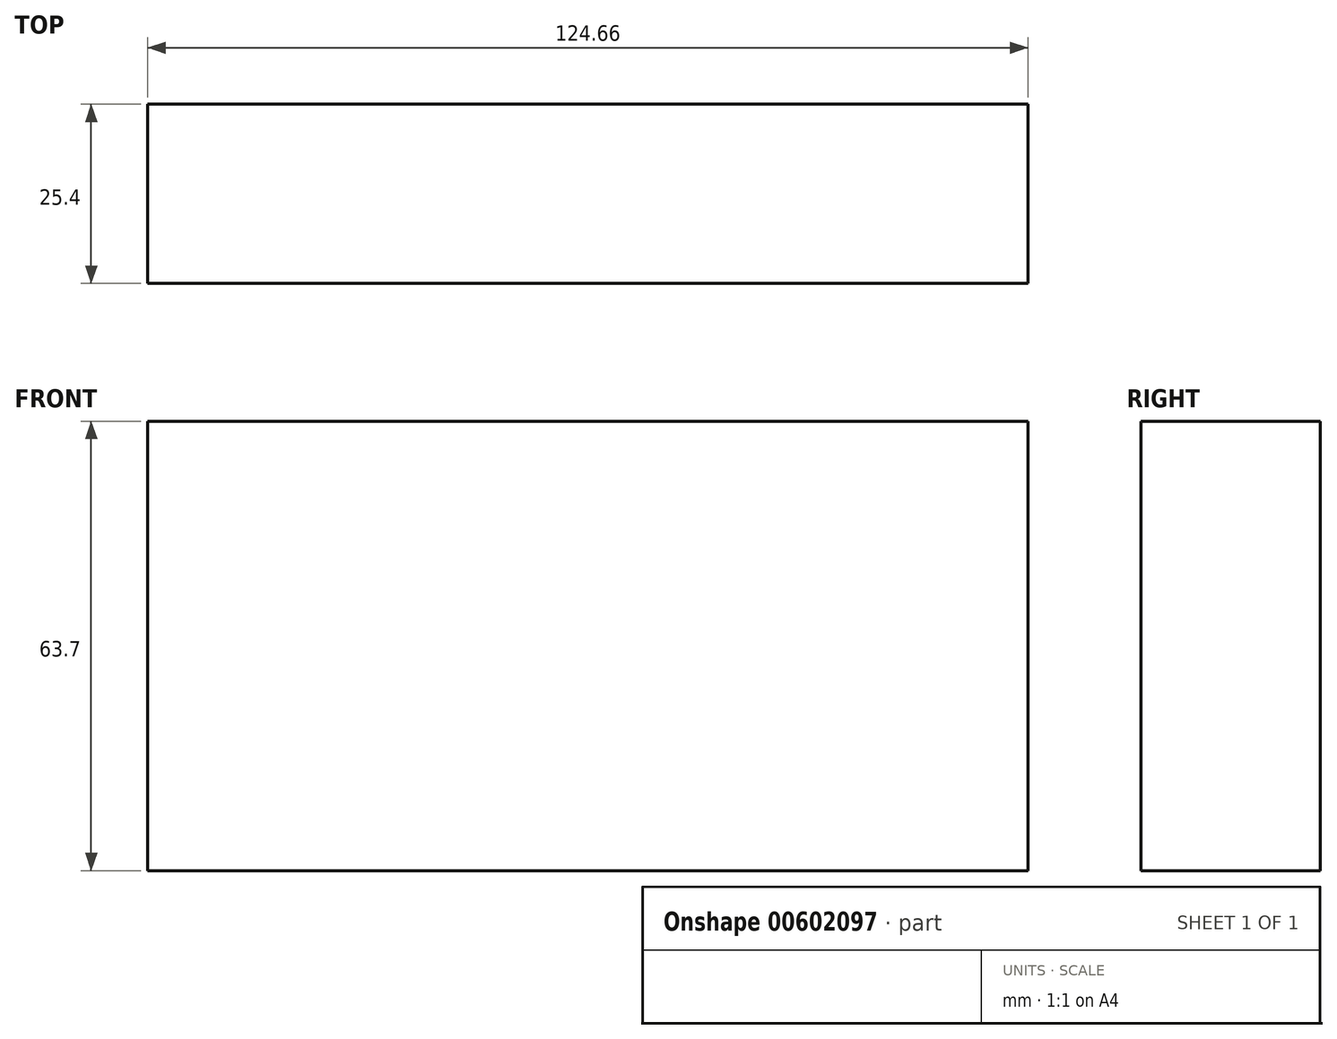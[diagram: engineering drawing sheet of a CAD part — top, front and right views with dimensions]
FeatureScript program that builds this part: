
annotation { "Feature Type Name" : "Feature", "Feature Type Description" : "" }
export const myFeature = defineFeature(function(context is Context, id is Id, definition is map)
    precondition{}
    {
        {
            var Q0;
            Q0=qCreatedBy(makeId("Front.planeOp"),FACE);
            var sketch = newSketch(context, id + "F0", { "sketchPlane" : qUnion([Q0])});
            skLineSegment(sketch, "E0.bottom", {"start": v(-55.32, 32.92) * mm, "end": v(69.34, 32.92) * mm});
            skLineSegment(sketch, "E0.top", {"start": v(-55.32, -30.78) * mm, "end": v(69.34, -30.78) * mm});
            skLineSegment(sketch, "E0.left", {"start": v(-55.32, 32.92) * mm, "end": v(-55.32, -30.78) * mm});
            skLineSegment(sketch, "E0.right", {"start": v(69.34, 32.92) * mm, "end": v(69.34, -30.78) * mm});
            skSolve(sketch);
        }
        {
            var Q0;
            Q0 = qSketchRegion(id + "F0", true);
            extrude(context, id + "F1", {"entities" : qUnion([Q0]), "depth" : 25.4 * mm, "offsetDistance" : 25.4 * mm});
        }
    });
